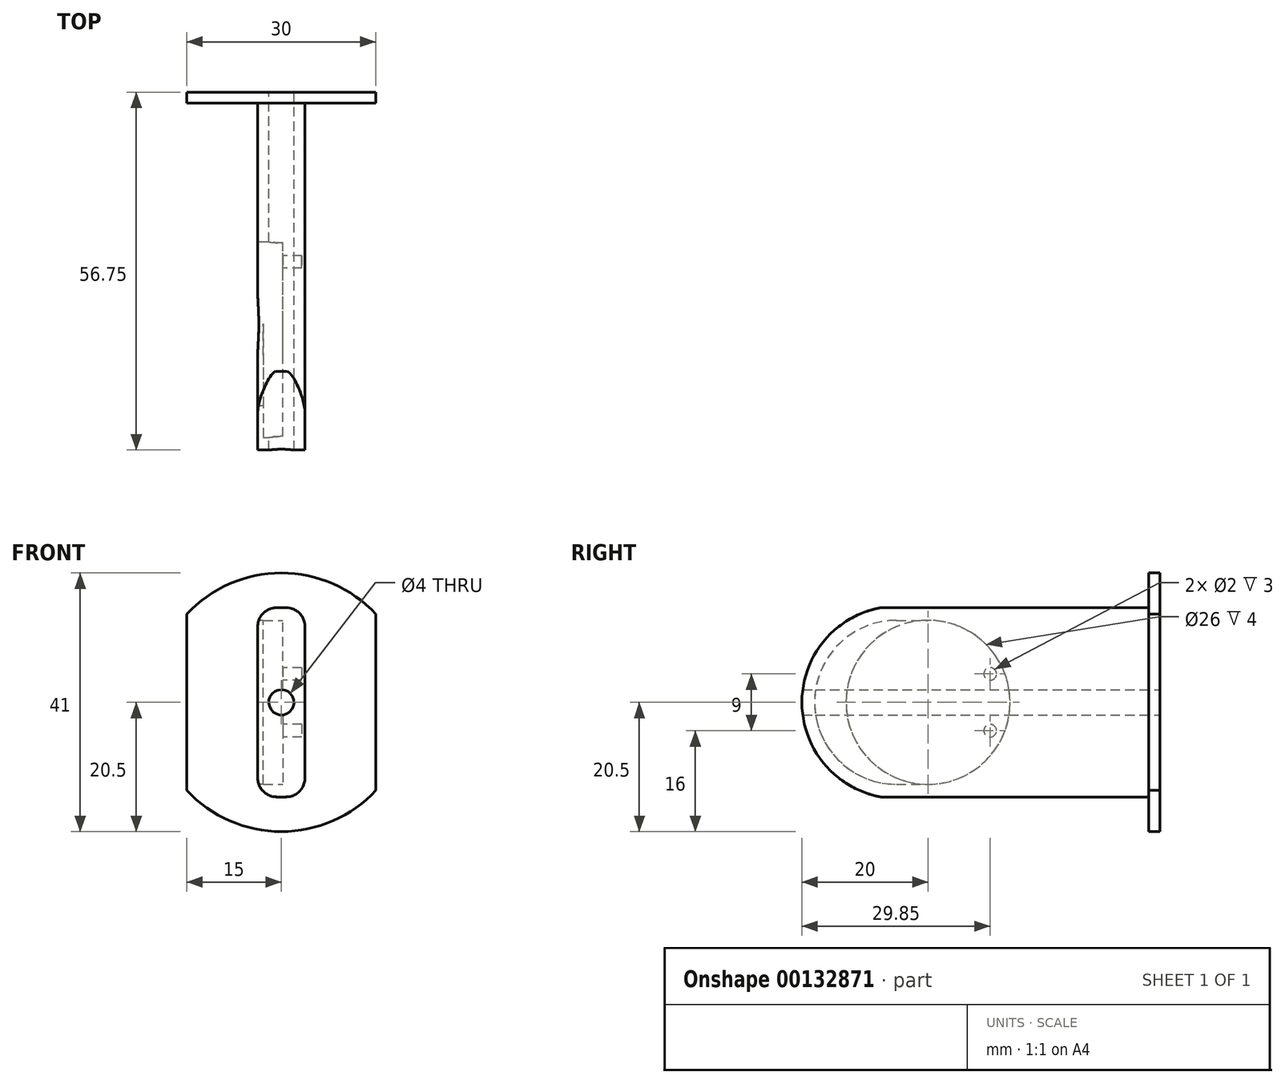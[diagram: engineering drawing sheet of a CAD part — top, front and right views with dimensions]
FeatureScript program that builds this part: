
annotation { "Feature Type Name" : "Feature", "Feature Type Description" : "" }
export const myFeature = defineFeature(function(context is Context, id is Id, definition is map)
    precondition{}
    {
        {
            var Q0;
            Q0=qCreatedBy(makeId("Front.planeOp"),FACE);
            var sketch = newSketch(context, id + "F0", { "sketchPlane" : qUnion([Q0])});
            skCircle(sketch, "E0", {"center": v(0, 0) * mm, "radius": 23 * mm});
            skSolve(sketch);
        }
        {
            var Q0;
            Q0=qSketchRegion(id+"F0",true);
            extrude(context, id + "F1", {"entities" : qUnion([Q0]), "depth" : 1.5 * mm});
        }
        {
            var Q0;
            Q0=makeQuery(id+"F1.opExtrude","CAP_FACE",FACE,{"disambiguationData":[OSD([sQuery(id+"F0.wireOp",EDGE,"E0")])],"isStart":false});
            var sketch = newSketch(context, id + "F2", { "sketchPlane" : qUnion([Q0])});
            skCircle(sketch, "E1", {"center": v(0, 0) * mm, "radius": 13 * mm});
            skCircle(sketch, "E2", {"center": v(0, 0) * mm, "radius": 14.5 * mm});
            skSolve(sketch);
        }
        {
            var Q0;
            Q0=qSketchRegion(id+"F2",true);
            extrude(context, id + "F3", {"entities" : qUnion([Q0]), "operationType" : NewBodyOperationType.ADD, "depth" : 5 * mm});
        }
        {
            var Q0;
            {var subQ0=sQuery(id+"F0.wireOp",EDGE,"E0");Q0=makeQuery(id+"F3.boolean.opBoolean","SPLIT",FACE,{"disambiguationData":[TD([makeQuery(id+"F1.opExtrude","SWEPT_FACE",FACE,{"disambiguationData":[OSD([subQ0])]})])],"derivedFrom":makeQuery(id+"F1.opExtrude","CAP_FACE",FACE,{"disambiguationData":[OSD([subQ0])],"isStart":false})});}
            var sketch = newSketch(context, id + "F4", { "sketchPlane" : qUnion([Q0])});
            skArc(sketch, "E3", {"start": v(7.49, 21.75) * mm, "mid": v(0, 23) * mm, "end": v(-7.49, 21.75) * mm});
            skArc(sketch, "E4", {"start": v(6.84, 19.86) * mm, "mid": v(0, 21) * mm, "end": v(-6.84, 19.86) * mm});
            skLineSegment(sketch, "E5", {"start": v(0, 30.17) * mm, "end": v(0, -31.06) * mm, "construction": true});
            skLineSegment(sketch, "E6", {"start": v(-6.84, 19.86) * mm, "end": v(-7.49, 21.75) * mm});
            skLineSegment(sketch, "E7", {"start": v(6.84, 19.86) * mm, "end": v(7.49, 21.75) * mm});
            skArc(sketch, "E8.1.0", {"start": v(-6.84, -19.86) * mm, "mid": v(0, -21) * mm, "end": v(6.84, -19.86) * mm});
            skArc(sketch, "E8.1.1", {"start": v(-7.49, -21.75) * mm, "mid": v(0, -23) * mm, "end": v(7.49, -21.75) * mm});
            skLineSegment(sketch, "E8.1.2", {"start": v(-6.84, -19.86) * mm, "end": v(-7.49, -21.75) * mm});
            skLineSegment(sketch, "E8.1.3", {"start": v(6.84, -19.86) * mm, "end": v(7.49, -21.75) * mm});
            skSolve(sketch);
        }
        {
            var Q0;
            Q0=qSketchRegion(id+"F4",true);
            extrude(context, id + "F5", {"entities" : qUnion([Q0]), "operationType" : NewBodyOperationType.ADD, "depth" : 25 * mm});
        }
        {
            var Q0;
            Q0=makeQuery(id+"F5.opExtrude","CAP_FACE",FACE,{"disambiguationData":[OSD([sQuery(id+"F4.wireOp",EDGE,"E8.1.0"),sQuery(id+"F4.wireOp",EDGE,"E8.1.1"),sQuery(id+"F4.wireOp",EDGE,"E8.1.2"),sQuery(id+"F4.wireOp",EDGE,"E8.1.3")])],"isStart":false});
            var sketch = newSketch(context, id + "F6", { "sketchPlane" : qUnion([Q0])});
            skCircle(sketch, "E9", {"center": v(0, 0) * mm, "radius": 23 * mm});
            skSolve(sketch);
        }
        {
            var Q0;
            Q0=qSketchRegion(id+"F6",true);
            extrude(context, id + "F7", {"entities" : qUnion([Q0]), "operationType" : NewBodyOperationType.ADD, "depth" : 1.75 * mm});
        }
        {
            var Q0;
            Q0=makeQuery(id+"F7.opExtrude","CAP_FACE",FACE,{"disambiguationData":[OSD([sQuery(id+"F6.wireOp",EDGE,"E9")])],"isStart":false});
            var sketch = newSketch(context, id + "F8", { "sketchPlane" : qUnion([Q0])});
            skLineSegment(sketch, "E10", {"start": v(-3.75, 12) * mm, "end": v(-3.75, -12) * mm});
            skLineSegment(sketch, "E11", {"start": v(3.75, 12) * mm, "end": v(3.75, -12) * mm});
            skLineSegment(sketch, "E12", {"start": v(0.75, -15) * mm, "end": v(-0.75, -15) * mm});
            skLineSegment(sketch, "E13", {"start": v(0.75, 15) * mm, "end": v(-0.75, 15) * mm});
            skPoint(sketch, "E14.visualSharp", {"position": v(-3.75, 15) * mm});
            skArc(sketch, "E14.filletArc", {"start": v(-0.75, 15) * mm, "mid": v(-2.87, 14.12) * mm, "end": v(-3.75, 12) * mm});
            skPoint(sketch, "E15.visualSharp", {"position": v(3.75, 15) * mm});
            skArc(sketch, "E15.filletArc", {"start": v(3.75, 12) * mm, "mid": v(2.87, 14.12) * mm, "end": v(0.75, 15) * mm});
            skPoint(sketch, "E16.visualSharp", {"position": v(-3.75, -15) * mm});
            skArc(sketch, "E16.filletArc", {"start": v(-3.75, -12) * mm, "mid": v(-2.87, -14.12) * mm, "end": v(-0.75, -15) * mm});
            skPoint(sketch, "E17.visualSharp", {"position": v(3.75, -15) * mm});
            skArc(sketch, "E17.filletArc", {"start": v(0.75, -15) * mm, "mid": v(2.87, -14.12) * mm, "end": v(3.75, -12) * mm});
            skSolve(sketch);
        }
        {
            var Q0;
            Q0=qSketchRegion(id+"F8",true);
            extrude(context, id + "F9", {"entities" : qUnion([Q0]), "operationType" : NewBodyOperationType.ADD, "depth" : 55 * mm});
        }
        {
            var Q0;
            Q0=makeQuery(id+"F9.opExtrude","SWEPT_FACE",FACE,{"disambiguationData":[OSD([sQuery(id+"F8.wireOp",EDGE,"E10")])]});
            var sketch = newSketch(context, id + "F10", { "sketchPlane" : qUnion([Q0])});
            skLineSegment(sketch, "E18", {"start": v(83.25, 22.76) * mm, "end": v(83.25, -17.15) * mm, "construction": true});
            skLineSegment(sketch, "E19", {"start": v(70.75, 22.76) * mm, "end": v(70.75, -17.15) * mm, "construction": true});
            skLineSegment(sketch, "E20", {"start": v(70.75, 15) * mm, "end": v(83.25, 15) * mm, "construction": true});
            skLineSegment(sketch, "E21", {"start": v(70.75, -15) * mm, "end": v(83.25, -15) * mm, "construction": true});
            skLineSegment(sketch, "E22", {"start": v(70.75, 0) * mm, "end": v(83.25, 0) * mm});
            skArc(sketch, "E23", {"start": v(70.75, -15) * mm, "mid": v(83.25, 0) * mm, "end": v(70.75, 15) * mm});
            skLineSegment(sketch, "E24", {"start": v(70.75, -15) * mm, "end": v(83.25, -15) * mm});
            skLineSegment(sketch, "E25", {"start": v(83.25, 0) * mm, "end": v(83.25, -15) * mm});
            skLineSegment(sketch, "E26", {"start": v(70.75, 15) * mm, "end": v(83.25, 15) * mm});
            skLineSegment(sketch, "E27", {"start": v(83.25, 15) * mm, "end": v(83.25, 0) * mm});
            skSolve(sketch);
        }
        {
            var Q0;
            Q0=qSketchRegion(id+"F10",true);
            extrude(context, id + "F11", {"entities" : qUnion([Q0]), "operationType" : NewBodyOperationType.REMOVE, "oppositeDirection" : true, "depth" : 25 * mm});
        }
        {
            var Q0;
            Q0=makeQuery(id+"F9.opExtrude","SWEPT_FACE",FACE,{"disambiguationData":[OSD([sQuery(id+"F8.wireOp",EDGE,"E10")])]});
            var sketch = newSketch(context, id + "F12", { "sketchPlane" : qUnion([Q0])});
            skArc(sketch, "E28", {"start": v(63.25, 13) * mm, "mid": v(50.25, 0) * mm, "end": v(63.25, -13) * mm});
            skArc(sketch, "E29", {"start": v(63.25, -13) * mm, "mid": v(76.25, 0) * mm, "end": v(63.25, 13) * mm});
            skSolve(sketch);
        }
        {
            var Q0;
            Q0=qSketchRegion(id+"F12",true);
            extrude(context, id + "F13", {"entities" : qUnion([Q0]), "operationType" : NewBodyOperationType.REMOVE, "oppositeDirection" : true, "depth" : 4 * mm});
        }
        {
            var Q0;
            Q0=makeQuery(id+"F7.opExtrude","CAP_FACE",FACE,{"disambiguationData":[OSD([sQuery(id+"F6.wireOp",EDGE,"E9")])],"isStart":true});
            var sketch = newSketch(context, id + "F14", { "sketchPlane" : qUnion([Q0])});
            skCircle(sketch, "E30", {"center": v(0, 0) * mm, "radius": 2 * mm});
            skSolve(sketch);
        }
        {
            var Q0;
            Q0=qSketchRegion(id+"F14",true);
            extrude(context, id + "F15", {"entities" : qUnion([Q0]), "operationType" : NewBodyOperationType.REMOVE, "oppositeDirection" : true, "depth" : 80 * mm});
        }
        {
            var Q0;
            Q0=makeQuery(id+"F15.boolean.opBoolean","SPLIT",FACE,{"disambiguationData":[OD(1.0)],"derivedFrom":makeQuery(id+"F13.boolean.opBoolean","COPY",FACE,{"derivedFrom":makeQuery(id+"F13.opExtrude","CAP_FACE",FACE,{"disambiguationData":[OSD([sQuery(id+"F12.wireOp",EDGE,"E28"),sQuery(id+"F12.wireOp",EDGE,"E29")])],"isStart":false})})});
            var sketch = newSketch(context, id + "F16", { "sketchPlane" : qUnion([Q0])});
            skArc(sketch, "E31", {"start": v(68.25, -13) * mm, "mid": v(81.25, 0) * mm, "end": v(68.25, 13) * mm});
            skLineSegment(sketch, "E32", {"start": v(68.25, 13) * mm, "end": v(63.25, 13) * mm});
            skLineSegment(sketch, "E33", {"start": v(68.25, -13) * mm, "end": v(63.25, -13) * mm});
            skArc(sketch, "E34", {"start": v(63.25, 13) * mm, "mid": v(50.25, 0) * mm, "end": v(63.25, -13) * mm});
            skSolve(sketch);
        }
        {
            var Q0;
            Q0=qSketchRegion(id+"F16",true);
            extrude(context, id + "F17", {"entities" : qUnion([Q0]), "operationType" : NewBodyOperationType.REMOVE, "depth" : 3.1 * mm});
        }
        {
            var Q0;
            Q0=makeQuery(id+"F1.opExtrude","CAP_FACE",FACE,{"disambiguationData":[OSD([sQuery(id+"F0.wireOp",EDGE,"E0")])],"isStart":true});
            var sketch = newSketch(context, id + "F18", { "sketchPlane" : qUnion([Q0])});
            skCircle(sketch, "E35", {"center": v(0, 0) * mm, "radius": 23 * mm});
            skSolve(sketch);
        }
        {
            var Q0;
            Q0 = qSketchRegion(id + "F18", true);
            extrude(context, id + "F19", {"entities" : qUnion([Q0]), "operationType" : NewBodyOperationType.REMOVE, "oppositeDirection" : true, "depth" : 26.5 * mm});
        }
        {
            var Q0;
            Q0=makeQuery(id+"F7.opExtrude","CAP_FACE",FACE,{"disambiguationData":[OSD([sQuery(id+"F6.wireOp",EDGE,"E9")])],"isStart":false});
            var sketch = newSketch(context, id + "F20", { "sketchPlane" : qUnion([Q0])});
            skArc(sketch, "E36", {"start": v(-15, 17.44) * mm, "mid": v(-23, 0) * mm, "end": v(-15, -17.44) * mm});
            skLineSegment(sketch, "E37", {"start": v(-15, 17.44) * mm, "end": v(-15, -17.44) * mm});
            skLineSegment(sketch, "E38", {"start": v(15, 17.44) * mm, "end": v(15, -17.44) * mm});
            skArc(sketch, "E39.trimOffspring", {"start": v(15, -17.44) * mm, "mid": v(23, 0) * mm, "end": v(15, 17.44) * mm});
            skSolve(sketch);
        }
        {
            var Q0;
            Q0 = qSketchRegion(id + "F20", true);
            extrude(context, id + "F21", {"entities" : qUnion([Q0]), "operationType" : NewBodyOperationType.REMOVE, "oppositeDirection" : true, "depth" : 25 * mm});
        }
        {
            var Q0;
            Q0=makeQuery(id+"F17.boolean.opBoolean","MERGE",FACE,{"derivedFrom":[makeQuery(id+"F15.boolean.opBoolean","SPLIT",FACE,{"disambiguationData":[OD(1.0)],"derivedFrom":makeQuery(id+"F13.boolean.opBoolean","COPY",FACE,{"derivedFrom":makeQuery(id+"F13.opExtrude","CAP_FACE",FACE,{"disambiguationData":[OSD([sQuery(id+"F12.wireOp",EDGE,"E28"),sQuery(id+"F12.wireOp",EDGE,"E29")])],"isStart":false})})}),makeQuery(id+"F17.opExtrude","CAP_FACE",FACE,{"disambiguationData":[OSD([sQuery(id+"F16.wireOp",EDGE,"E31"),sQuery(id+"F16.wireOp",EDGE,"E32"),sQuery(id+"F16.wireOp",EDGE,"E33"),sQuery(id+"F16.wireOp",EDGE,"E34")])],"isStart":true})]});
            var sketch = newSketch(context, id + "F22", { "sketchPlane" : qUnion([Q0])});
            skCircle(sketch, "E40", {"center": v(63.25, 0) * mm, "radius": 13 * mm, "construction": true});
            skCircle(sketch, "E41", {"center": v(68.25, 0) * mm, "radius": 13 * mm, "construction": true});
            skCircle(sketch, "E42", {"center": v(53.4, 4.5) * mm, "radius": 1 * mm});
            skLineSegment(sketch, "E43", {"start": v(26.43, 0) * mm, "end": v(110.52, 0) * mm, "construction": true});
            skCircle(sketch, "E44.MirrorC", {"center": v(53.4, -4.5) * mm, "radius": 1 * mm});
            skSolve(sketch);
        }
        {
            var Q0;
            Q0 = qSketchRegion(id + "F22", true);
            extrude(context, id + "F23", {"entities" : qUnion([Q0]), "operationType" : NewBodyOperationType.REMOVE, "oppositeDirection" : true, "depth" : 3 * mm});
        }
        {
            var Q0;
            Q0=makeQuery(id+"F7.opExtrude","CAP_FACE",FACE,{"disambiguationData":[OSD([sQuery(id+"F6.wireOp",EDGE,"E9")])],"isStart":false});
            var sketch = newSketch(context, id + "F24", { "sketchPlane" : qUnion([Q0])});
            skArc(sketch, "E45", {"start": v(-15, -13.97) * mm, "mid": v(0, -20.5) * mm, "end": v(15, -13.97) * mm});
            skLineSegment(sketch, "E46", {"start": v(-15, 13.97) * mm, "end": v(-15, -13.97) * mm});
            skArc(sketch, "E47", {"start": v(-15, -17.44) * mm, "mid": v(0, -23) * mm, "end": v(15, -17.44) * mm});
            skLineSegment(sketch, "E48", {"start": v(-15, 17.44) * mm, "end": v(-15, 13.97) * mm});
            skLineSegment(sketch, "E49.trimOffspring", {"start": v(-15, -13.97) * mm, "end": v(-15, -17.44) * mm});
            skLineSegment(sketch, "E50", {"start": v(15, 17.44) * mm, "end": v(15, -17.44) * mm});
            skArc(sketch, "E51.trimOffspring", {"start": v(15, 17.44) * mm, "mid": v(0, 23) * mm, "end": v(-15, 17.44) * mm});
            skArc(sketch, "E52.trimOffspring", {"start": v(15, 13.97) * mm, "mid": v(0, 20.5) * mm, "end": v(-15, 13.97) * mm});
            skSolve(sketch);
        }
        {
            var Q0;
            Q0=makeQuery(id+"F24.imprint","IMPRINT",FACE,{"disambiguationData":[TD([[makeQuery(id+"F24.imprint","IMPRINT",EDGE,{"derivedFrom":sQuery(id+"F24.wireOp",EDGE,"E48")}),1.0]])]});
            var Q1;
            {var subQ0=sQuery(id+"F24.wireOp",EDGE,"E45");Q1=makeQuery(id+"F24.imprint","IMPRINT",FACE,{"disambiguationData":[TD([[makeQuery(id+"F24.imprint","IMPRINT",EDGE,{"derivedFrom":subQ0}),-1.0]])]});}
            extrude(context, id + "F25", {"entities" : qUnion([Q0, Q1]), "operationType" : NewBodyOperationType.REMOVE, "oppositeDirection" : true, "depth" : 25 * mm});
        }
    });
